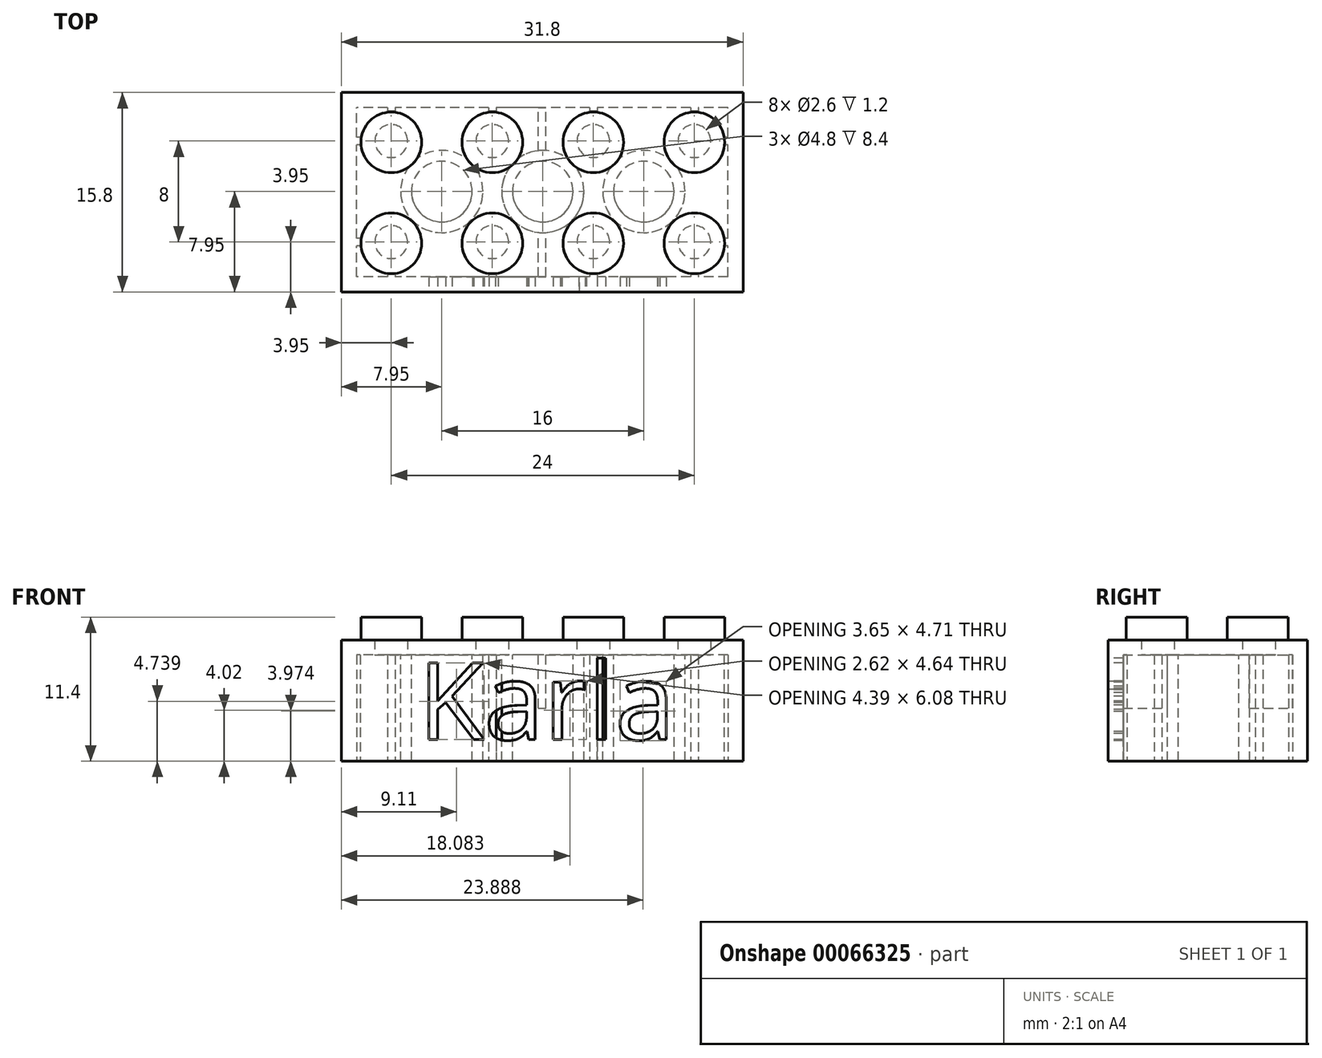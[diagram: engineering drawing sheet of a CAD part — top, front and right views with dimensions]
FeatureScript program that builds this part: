
annotation { "Feature Type Name" : "Feature", "Feature Type Description" : "" }
export const myFeature = defineFeature(function(context is Context, id is Id, definition is map)
    precondition{}
    {
        {
            var Q0;
            Q0=qCreatedBy(makeId("Top.planeOp"),FACE);
            var sketch = newSketch(context, id + "F0", { "sketchPlane" : qUnion([Q0])});
            skLineSegment(sketch, "E0.rect.bottom", {"start": v(15.9, 7.9) * mm, "end": v(-15.9, 7.9) * mm});
            skLineSegment(sketch, "E0.rect.top", {"start": v(15.9, -7.9) * mm, "end": v(-15.9, -7.9) * mm});
            skLineSegment(sketch, "E0.rect.left", {"start": v(15.9, 7.9) * mm, "end": v(15.9, -7.9) * mm});
            skLineSegment(sketch, "E0.rect.right", {"start": v(-15.9, 7.9) * mm, "end": v(-15.9, -7.9) * mm});
            skPoint(sketch, "E0.rect.middle", {"position": v(0, 0) * mm});
            skSolve(sketch);
        }
        {
            var Q0;
            Q0 = qSketchRegion(id + "F0", true);
            extrude(context, id + "F1", {"entities" : qUnion([Q0]), "depth" : 9.6 * mm});
        }
        {
            var Q0;
            Q0=makeQuery(id+"F1.opExtrude","CAP_FACE",FACE,{"disambiguationData":[OSD([sQuery(id+"F0.wireOp",EDGE,"E0.rect.bottom"),sQuery(id+"F0.wireOp",EDGE,"E0.rect.top"),sQuery(id+"F0.wireOp",EDGE,"E0.rect.left"),sQuery(id+"F0.wireOp",EDGE,"E0.rect.right")])],"isStart":true});
            var sketch = newSketch(context, id + "F2", { "sketchPlane" : qUnion([Q0])});
            skLineSegment(sketch, "E1.rect.bottom", {"start": v(14.7, 6.7) * mm, "end": v(-14.7, 6.7) * mm});
            skLineSegment(sketch, "E1.rect.top", {"start": v(14.7, -6.7) * mm, "end": v(-14.7, -6.7) * mm});
            skLineSegment(sketch, "E1.rect.left", {"start": v(14.7, 6.7) * mm, "end": v(14.7, -6.7) * mm});
            skLineSegment(sketch, "E1.rect.right", {"start": v(-14.7, 6.7) * mm, "end": v(-14.7, -6.7) * mm});
            skPoint(sketch, "E1.rect.middle", {"position": v(0, 0) * mm});
            skSolve(sketch);
        }
        {
            var Q0;
            Q0 = qSketchRegion(id + "F2", true);
            extrude(context, id + "F3", {"entities" : qUnion([Q0]), "operationType" : NewBodyOperationType.REMOVE, "oppositeDirection" : true, "depth" : 8.4 * mm});
        }
        {
            var Q0;
            Q0=makeQuery(id+"F1.opExtrude","CAP_FACE",FACE,{"disambiguationData":[OSD([sQuery(id+"F0.wireOp",EDGE,"E0.rect.bottom"),sQuery(id+"F0.wireOp",EDGE,"E0.rect.top"),sQuery(id+"F0.wireOp",EDGE,"E0.rect.left"),sQuery(id+"F0.wireOp",EDGE,"E0.rect.right")])],"isStart":false});
            var sketch = newSketch(context, id + "F4", { "sketchPlane" : qUnion([Q0])});
            skLineSegment(sketch, "E2", {"start": v(-26.48, 0) * mm, "end": v(22.09, 0) * mm, "construction": true});
            skCircle(sketch, "E3", {"center": v(-11.95, 3.95) * mm, "radius": 2.4 * mm});
            skCircle(sketch, "E4.0.1.0", {"center": v(-11.95, -4.05) * mm, "radius": 2.4 * mm});
            skCircle(sketch, "E4.1.0.0", {"center": v(-3.95, 3.95) * mm, "radius": 2.4 * mm});
            skCircle(sketch, "E4.1.1.0", {"center": v(-3.95, -4.05) * mm, "radius": 2.4 * mm});
            skCircle(sketch, "E4.2.0.0", {"center": v(4.05, 3.95) * mm, "radius": 2.4 * mm});
            skCircle(sketch, "E4.2.1.0", {"center": v(4.05, -4.05) * mm, "radius": 2.4 * mm});
            skCircle(sketch, "E4.3.0.0", {"center": v(12.05, 3.95) * mm, "radius": 2.4 * mm});
            skCircle(sketch, "E4.3.1.0", {"center": v(12.05, -4.05) * mm, "radius": 2.4 * mm});
            skLineSegment(sketch, "E4.direction1", {"start": v(-11.95, 3.95) * mm, "end": v(-3.95, 3.95) * mm, "construction": true});
            skLineSegment(sketch, "E4.direction2", {"start": v(-11.95, 3.95) * mm, "end": v(-11.95, -4.05) * mm, "construction": true});
            skSolve(sketch);
        }
        {
            var Q0;
            Q0 = qSketchRegion(id + "F4", true);
            extrude(context, id + "F5", {"entities" : qUnion([Q0]), "operationType" : NewBodyOperationType.ADD, "depth" : 1.8 * mm});
        }
        {
            var Q0;
            Q0=makeQuery(id+"F3.boolean.opBoolean","COPY",FACE,{"derivedFrom":makeQuery(id+"F3.opExtrude","CAP_FACE",FACE,{"disambiguationData":[OSD([sQuery(id+"F2.wireOp",EDGE,"E1.rect.bottom"),sQuery(id+"F2.wireOp",EDGE,"E1.rect.top"),sQuery(id+"F2.wireOp",EDGE,"E1.rect.left"),sQuery(id+"F2.wireOp",EDGE,"E1.rect.right")])],"isStart":false})});
            var sketch = newSketch(context, id + "F6", { "sketchPlane" : qUnion([Q0])});
            skCircle(sketch, "E5", {"center": v(-11.95, 3.95) * mm, "radius": 1.3 * mm});
            skCircle(sketch, "E6.0.1.0", {"center": v(-11.95, -4.05) * mm, "radius": 1.3 * mm});
            skCircle(sketch, "E6.1.0.0", {"center": v(-3.95, 3.95) * mm, "radius": 1.3 * mm});
            skCircle(sketch, "E6.1.1.0", {"center": v(-3.95, -4.05) * mm, "radius": 1.3 * mm});
            skCircle(sketch, "E6.2.0.0", {"center": v(4.05, 3.95) * mm, "radius": 1.3 * mm});
            skCircle(sketch, "E6.2.1.0", {"center": v(4.05, -4.05) * mm, "radius": 1.3 * mm});
            skCircle(sketch, "E6.3.0.0", {"center": v(12.05, 3.95) * mm, "radius": 1.3 * mm});
            skCircle(sketch, "E6.3.1.0", {"center": v(12.05, -4.05) * mm, "radius": 1.3 * mm});
            skLineSegment(sketch, "E6.direction1", {"start": v(-11.95, 3.95) * mm, "end": v(-3.95, 3.95) * mm, "construction": true});
            skLineSegment(sketch, "E6.direction2", {"start": v(-11.95, 3.95) * mm, "end": v(-11.95, -4.05) * mm, "construction": true});
            skSolve(sketch);
        }
        {
            var Q0;
            Q0 = qSketchRegion(id + "F6", true);
            extrude(context, id + "F7", {"entities" : qUnion([Q0]), "operationType" : NewBodyOperationType.REMOVE, "oppositeDirection" : true, "depth" : 1.2 * mm});
        }
        {
            var Q0;
            Q0=makeQuery(id+"F3.boolean.opBoolean","COPY",FACE,{"derivedFrom":makeQuery(id+"F3.opExtrude","CAP_FACE",FACE,{"disambiguationData":[OSD([sQuery(id+"F2.wireOp",EDGE,"E1.rect.bottom"),sQuery(id+"F2.wireOp",EDGE,"E1.rect.top"),sQuery(id+"F2.wireOp",EDGE,"E1.rect.left"),sQuery(id+"F2.wireOp",EDGE,"E1.rect.right")])],"isStart":false})});
            var sketch = newSketch(context, id + "F8", { "sketchPlane" : qUnion([Q0])});
            skLineSegment(sketch, "E7", {"start": v(-11.95, 3.95) * mm, "end": v(-3.95, -4.05) * mm, "construction": true});
            skLineSegment(sketch, "E8", {"start": v(-3.95, 3.95) * mm, "end": v(-11.95, -4.05) * mm, "construction": true});
            skLineSegment(sketch, "E9", {"start": v(4.05, 3.95) * mm, "end": v(12.05, -4.05) * mm, "construction": true});
            skLineSegment(sketch, "E10", {"start": v(4.05, -4.05) * mm, "end": v(12.05, 3.95) * mm, "construction": true});
            skLineSegment(sketch, "E11", {"start": v(-3.95, 3.95) * mm, "end": v(4.05, -4.05) * mm, "construction": true});
            skLineSegment(sketch, "E12", {"start": v(-3.95, -4.05) * mm, "end": v(4.05, 3.95) * mm, "construction": true});
            skCircle(sketch, "E13", {"center": v(-7.95, -0.05) * mm, "radius": 2.4 * mm});
            skCircle(sketch, "E14", {"center": v(-7.95, -0.05) * mm, "radius": 3.25 * mm});
            skCircle(sketch, "E15", {"center": v(0.05, -0.05) * mm, "radius": 2.4 * mm});
            skCircle(sketch, "E16", {"center": v(0.05, -0.05) * mm, "radius": 3.25 * mm});
            skCircle(sketch, "E17", {"center": v(8.05, -0.05) * mm, "radius": 2.4 * mm});
            skCircle(sketch, "E18", {"center": v(8.05, -0.05) * mm, "radius": 3.25 * mm});
            skSolve(sketch);
        }
        {
            var Q0;
            Q0 = qSketchRegion(id + "F8", true);
            var Q1;
            Q1=makeQuery(id+"F1.opExtrude","CAP_FACE",FACE,{"disambiguationData":[OSD([sQuery(id+"F0.wireOp",EDGE,"E0.rect.bottom"),sQuery(id+"F0.wireOp",EDGE,"E0.rect.top"),sQuery(id+"F0.wireOp",EDGE,"E0.rect.left"),sQuery(id+"F0.wireOp",EDGE,"E0.rect.right")])],"isStart":true});
            extrude(context, id + "F9", {"entities" : qUnion([Q0]), "operationType" : NewBodyOperationType.ADD, "endBound" : BoundingType.UP_TO_SURFACE, "endBoundEntityFace" : qUnion([Q1]), "depth" : 25 * mm});
        }
        {
            var Q0;
            Q0=makeQuery(id+"F1.opExtrude","CAP_FACE",FACE,{"disambiguationData":[OSD([sQuery(id+"F0.wireOp",EDGE,"E0.rect.bottom"),sQuery(id+"F0.wireOp",EDGE,"E0.rect.top"),sQuery(id+"F0.wireOp",EDGE,"E0.rect.left"),sQuery(id+"F0.wireOp",EDGE,"E0.rect.right")])],"isStart":true});
            var sketch = newSketch(context, id + "F10", { "sketchPlane" : qUnion([Q0])});
            skLineSegment(sketch, "E19.bottom", {"start": v(-12.25, 6.7) * mm, "end": v(-11.65, 6.7) * mm});
            skLineSegment(sketch, "E19.top", {"start": v(-12.25, 6.4) * mm, "end": v(-11.65, 6.4) * mm});
            skLineSegment(sketch, "E19.left", {"start": v(-12.25, 6.7) * mm, "end": v(-12.25, 6.4) * mm});
            skLineSegment(sketch, "E19.right", {"start": v(-11.65, 6.7) * mm, "end": v(-11.65, 6.4) * mm});
            skLineSegment(sketch, "E20.0.1.0", {"start": v(-12.25, -6.4) * mm, "end": v(-11.65, -6.4) * mm});
            skLineSegment(sketch, "E20.0.1.1", {"start": v(-12.25, -6.4) * mm, "end": v(-12.25, -6.7) * mm});
            skLineSegment(sketch, "E20.0.1.2", {"start": v(-12.25, -6.7) * mm, "end": v(-11.65, -6.7) * mm});
            skLineSegment(sketch, "E20.0.1.3", {"start": v(-11.65, -6.4) * mm, "end": v(-11.65, -6.7) * mm});
            skLineSegment(sketch, "E20.1.0.0", {"start": v(-4.25, 6.7) * mm, "end": v(-3.65, 6.7) * mm});
            skLineSegment(sketch, "E20.1.0.1", {"start": v(-4.25, 6.7) * mm, "end": v(-4.25, 6.4) * mm});
            skLineSegment(sketch, "E20.1.0.2", {"start": v(-4.25, 6.4) * mm, "end": v(-3.65, 6.4) * mm});
            skLineSegment(sketch, "E20.1.0.3", {"start": v(-3.65, 6.7) * mm, "end": v(-3.65, 6.4) * mm});
            skLineSegment(sketch, "E20.1.1.0", {"start": v(-4.25, -6.4) * mm, "end": v(-3.65, -6.4) * mm});
            skLineSegment(sketch, "E20.1.1.1", {"start": v(-4.25, -6.4) * mm, "end": v(-4.25, -6.7) * mm});
            skLineSegment(sketch, "E20.1.1.2", {"start": v(-4.25, -6.7) * mm, "end": v(-3.65, -6.7) * mm});
            skLineSegment(sketch, "E20.1.1.3", {"start": v(-3.65, -6.4) * mm, "end": v(-3.65, -6.7) * mm});
            skLineSegment(sketch, "E20.2.0.0", {"start": v(3.75, 6.7) * mm, "end": v(4.35, 6.7) * mm});
            skLineSegment(sketch, "E20.2.0.1", {"start": v(3.75, 6.7) * mm, "end": v(3.75, 6.4) * mm});
            skLineSegment(sketch, "E20.2.0.2", {"start": v(3.75, 6.4) * mm, "end": v(4.35, 6.4) * mm});
            skLineSegment(sketch, "E20.2.0.3", {"start": v(4.35, 6.7) * mm, "end": v(4.35, 6.4) * mm});
            skLineSegment(sketch, "E20.2.1.0", {"start": v(3.75, -6.4) * mm, "end": v(4.35, -6.4) * mm});
            skLineSegment(sketch, "E20.2.1.1", {"start": v(3.75, -6.4) * mm, "end": v(3.75, -6.7) * mm});
            skLineSegment(sketch, "E20.2.1.2", {"start": v(3.75, -6.7) * mm, "end": v(4.35, -6.7) * mm});
            skLineSegment(sketch, "E20.2.1.3", {"start": v(4.35, -6.4) * mm, "end": v(4.35, -6.7) * mm});
            skLineSegment(sketch, "E20.3.0.0", {"start": v(11.75, 6.7) * mm, "end": v(12.35, 6.7) * mm});
            skLineSegment(sketch, "E20.3.0.1", {"start": v(11.75, 6.7) * mm, "end": v(11.75, 6.4) * mm});
            skLineSegment(sketch, "E20.3.0.2", {"start": v(11.75, 6.4) * mm, "end": v(12.35, 6.4) * mm});
            skLineSegment(sketch, "E20.3.0.3", {"start": v(12.35, 6.7) * mm, "end": v(12.35, 6.4) * mm});
            skLineSegment(sketch, "E20.3.1.0", {"start": v(11.75, -6.4) * mm, "end": v(12.35, -6.4) * mm});
            skLineSegment(sketch, "E20.3.1.1", {"start": v(11.75, -6.4) * mm, "end": v(11.75, -6.7) * mm});
            skLineSegment(sketch, "E20.3.1.2", {"start": v(11.75, -6.7) * mm, "end": v(12.35, -6.7) * mm});
            skLineSegment(sketch, "E20.3.1.3", {"start": v(12.35, -6.4) * mm, "end": v(12.35, -6.7) * mm});
            skLineSegment(sketch, "E20.direction1", {"start": v(-12.25, 6.7) * mm, "end": v(-4.25, 6.7) * mm, "construction": true});
            skLineSegment(sketch, "E20.direction2", {"start": v(-12.25, 6.7) * mm, "end": v(-12.25, -6.4) * mm, "construction": true});
            skSolve(sketch);
        }
        {
            var Q0;
            Q0 = qSketchRegion(id + "F10", true);
            var Q1;
            {var subQ0=sQuery(id+"F2.wireOp",EDGE,"E1.rect.bottom");var subQ1=sQuery(id+"F2.wireOp",EDGE,"E1.rect.top");var subQ2=sQuery(id+"F2.wireOp",EDGE,"E1.rect.left");var subQ3=sQuery(id+"F2.wireOp",EDGE,"E1.rect.right");Q1=makeQuery(id+"F9.boolean.opBoolean","SPLIT",FACE,{"disambiguationData":[TD([makeQuery(id+"F3.boolean.opBoolean","COPY",FACE,{"derivedFrom":makeQuery(id+"F3.opExtrude","SWEPT_FACE",FACE,{"disambiguationData":[OSD([subQ0])]})})])],"derivedFrom":makeQuery(id+"F3.boolean.opBoolean","COPY",FACE,{"derivedFrom":makeQuery(id+"F3.opExtrude","CAP_FACE",FACE,{"disambiguationData":[OSD([subQ0,subQ1,subQ2,subQ3])],"isStart":false})})});}
            extrude(context, id + "F11", {"entities" : qUnion([Q0]), "operationType" : NewBodyOperationType.ADD, "endBound" : BoundingType.UP_TO_SURFACE, "oppositeDirection" : true, "endBoundEntityFace" : qUnion([Q1]), "depth" : 25 * mm});
        }
        {
            var Q0;
            Q0=makeQuery(id+"F11.boolean.opBoolean","MERGE",FACE,{"derivedFrom":[makeQuery(id+"F1.opExtrude","CAP_FACE",FACE,{"disambiguationData":[OSD([sQuery(id+"F0.wireOp",EDGE,"E0.rect.bottom"),sQuery(id+"F0.wireOp",EDGE,"E0.rect.top"),sQuery(id+"F0.wireOp",EDGE,"E0.rect.left"),sQuery(id+"F0.wireOp",EDGE,"E0.rect.right")])],"isStart":true}),makeQuery(id+"F11.opExtrude","CAP_FACE",FACE,{"disambiguationData":[OSD([sQuery(id+"F10.wireOp",EDGE,"E19.bottom"),sQuery(id+"F10.wireOp",EDGE,"E19.top"),sQuery(id+"F10.wireOp",EDGE,"E19.left"),sQuery(id+"F10.wireOp",EDGE,"E19.right")])],"isStart":true}),makeQuery(id+"F11.opExtrude","CAP_FACE",FACE,{"disambiguationData":[OSD([sQuery(id+"F10.wireOp",EDGE,"E20.0.1.0"),sQuery(id+"F10.wireOp",EDGE,"E20.0.1.1"),sQuery(id+"F10.wireOp",EDGE,"E20.0.1.2"),sQuery(id+"F10.wireOp",EDGE,"E20.0.1.3")])],"isStart":true}),makeQuery(id+"F11.opExtrude","CAP_FACE",FACE,{"disambiguationData":[OSD([sQuery(id+"F10.wireOp",EDGE,"E20.1.0.0"),sQuery(id+"F10.wireOp",EDGE,"E20.1.0.1"),sQuery(id+"F10.wireOp",EDGE,"E20.1.0.2"),sQuery(id+"F10.wireOp",EDGE,"E20.1.0.3")])],"isStart":true}),makeQuery(id+"F11.opExtrude","CAP_FACE",FACE,{"disambiguationData":[OSD([sQuery(id+"F10.wireOp",EDGE,"E20.1.1.0"),sQuery(id+"F10.wireOp",EDGE,"E20.1.1.1"),sQuery(id+"F10.wireOp",EDGE,"E20.1.1.2"),sQuery(id+"F10.wireOp",EDGE,"E20.1.1.3")])],"isStart":true}),makeQuery(id+"F11.opExtrude","CAP_FACE",FACE,{"disambiguationData":[OSD([sQuery(id+"F10.wireOp",EDGE,"E20.2.0.0"),sQuery(id+"F10.wireOp",EDGE,"E20.2.0.1"),sQuery(id+"F10.wireOp",EDGE,"E20.2.0.2"),sQuery(id+"F10.wireOp",EDGE,"E20.2.0.3")])],"isStart":true}),makeQuery(id+"F11.opExtrude","CAP_FACE",FACE,{"disambiguationData":[OSD([sQuery(id+"F10.wireOp",EDGE,"E20.2.1.0"),sQuery(id+"F10.wireOp",EDGE,"E20.2.1.1"),sQuery(id+"F10.wireOp",EDGE,"E20.2.1.2"),sQuery(id+"F10.wireOp",EDGE,"E20.2.1.3")])],"isStart":true}),makeQuery(id+"F11.opExtrude","CAP_FACE",FACE,{"disambiguationData":[OSD([sQuery(id+"F10.wireOp",EDGE,"E20.3.0.0"),sQuery(id+"F10.wireOp",EDGE,"E20.3.0.1"),sQuery(id+"F10.wireOp",EDGE,"E20.3.0.2"),sQuery(id+"F10.wireOp",EDGE,"E20.3.0.3")])],"isStart":true}),makeQuery(id+"F11.opExtrude","CAP_FACE",FACE,{"disambiguationData":[OSD([sQuery(id+"F10.wireOp",EDGE,"E20.3.1.0"),sQuery(id+"F10.wireOp",EDGE,"E20.3.1.1"),sQuery(id+"F10.wireOp",EDGE,"E20.3.1.2"),sQuery(id+"F10.wireOp",EDGE,"E20.3.1.3")])],"isStart":true})]});
            var sketch = newSketch(context, id + "F12", { "sketchPlane" : qUnion([Q0])});
            skLineSegment(sketch, "E21.bottom", {"start": v(-14.7, 4.25) * mm, "end": v(-14.4, 4.25) * mm});
            skLineSegment(sketch, "E21.top", {"start": v(-14.7, 3.65) * mm, "end": v(-14.4, 3.65) * mm});
            skLineSegment(sketch, "E21.left", {"start": v(-14.7, 4.25) * mm, "end": v(-14.7, 3.65) * mm});
            skLineSegment(sketch, "E21.right", {"start": v(-14.4, 4.25) * mm, "end": v(-14.4, 3.65) * mm});
            skLineSegment(sketch, "E22.0.1.0", {"start": v(-14.7, -3.75) * mm, "end": v(-14.7, -4.35) * mm});
            skLineSegment(sketch, "E22.0.1.1", {"start": v(-14.7, -3.75) * mm, "end": v(-14.4, -3.75) * mm});
            skLineSegment(sketch, "E22.0.1.2", {"start": v(-14.4, -3.75) * mm, "end": v(-14.4, -4.35) * mm});
            skLineSegment(sketch, "E22.0.1.3", {"start": v(-14.7, -4.35) * mm, "end": v(-14.4, -4.35) * mm});
            skLineSegment(sketch, "E22.1.0.0", {"start": v(14.4, 4.25) * mm, "end": v(14.4, 3.65) * mm});
            skLineSegment(sketch, "E22.1.0.1", {"start": v(14.4, 4.25) * mm, "end": v(14.7, 4.25) * mm});
            skLineSegment(sketch, "E22.1.0.2", {"start": v(14.7, 4.25) * mm, "end": v(14.7, 3.65) * mm});
            skLineSegment(sketch, "E22.1.0.3", {"start": v(14.4, 3.65) * mm, "end": v(14.7, 3.65) * mm});
            skLineSegment(sketch, "E22.1.1.0", {"start": v(14.4, -3.75) * mm, "end": v(14.4, -4.35) * mm});
            skLineSegment(sketch, "E22.1.1.1", {"start": v(14.4, -3.75) * mm, "end": v(14.7, -3.75) * mm});
            skLineSegment(sketch, "E22.1.1.2", {"start": v(14.7, -3.75) * mm, "end": v(14.7, -4.35) * mm});
            skLineSegment(sketch, "E22.1.1.3", {"start": v(14.4, -4.35) * mm, "end": v(14.7, -4.35) * mm});
            skLineSegment(sketch, "E22.direction1", {"start": v(-14.7, 3.65) * mm, "end": v(14.4, 3.65) * mm, "construction": true});
            skLineSegment(sketch, "E22.direction2", {"start": v(-14.7, 3.65) * mm, "end": v(-14.7, -4.35) * mm, "construction": true});
            skSolve(sketch);
        }
        {
            var Q0;
            Q0 = qSketchRegion(id + "F12", true);
            var Q1;
            {var subQ0=sQuery(id+"F2.wireOp",EDGE,"E1.rect.bottom");var subQ1=sQuery(id+"F2.wireOp",EDGE,"E1.rect.top");var subQ2=sQuery(id+"F2.wireOp",EDGE,"E1.rect.left");var subQ3=sQuery(id+"F2.wireOp",EDGE,"E1.rect.right");Q1=makeQuery(id+"F9.boolean.opBoolean","SPLIT",FACE,{"disambiguationData":[TD([makeQuery(id+"F3.boolean.opBoolean","COPY",FACE,{"derivedFrom":makeQuery(id+"F3.opExtrude","SWEPT_FACE",FACE,{"disambiguationData":[OSD([subQ0])]})})])],"derivedFrom":makeQuery(id+"F3.boolean.opBoolean","COPY",FACE,{"derivedFrom":makeQuery(id+"F3.opExtrude","CAP_FACE",FACE,{"disambiguationData":[OSD([subQ0,subQ1,subQ2,subQ3])],"isStart":false})})});}
            extrude(context, id + "F13", {"entities" : qUnion([Q0]), "operationType" : NewBodyOperationType.ADD, "endBound" : BoundingType.UP_TO_SURFACE, "oppositeDirection" : true, "endBoundEntityFace" : qUnion([Q1]), "depth" : 25 * mm});
        }
        {
            var Q0;
            Q0=makeQuery(id+"F8.imprint","IMPRINT",FACE,{"disambiguationData":[TD([[makeQuery(id+"F8.imprint","IMPRINT",EDGE,{"derivedFrom":sQuery(id+"F8.wireOp",EDGE,"E14")}),-1.0]])]});
            var sketch = newSketch(context, id + "F14", { "sketchPlane" : qUnion([Q0])});
            skLineSegment(sketch, "E23.bottom", {"start": v(-0.3, 6.95) * mm, "end": v(0.3, 6.95) * mm});
            skLineSegment(sketch, "E23.top", {"start": v(-0.3, 2.7) * mm, "end": v(0.3, 2.7) * mm});
            skLineSegment(sketch, "E23.left", {"start": v(-0.3, 6.95) * mm, "end": v(-0.3, 2.7) * mm});
            skLineSegment(sketch, "E23.right", {"start": v(0.3, 6.95) * mm, "end": v(0.3, 2.7) * mm});
            skLineSegment(sketch, "E24.bottom", {"start": v(-0.3, -2.7) * mm, "end": v(0.3, -2.7) * mm});
            skLineSegment(sketch, "E24.top", {"start": v(-0.3, -6.95) * mm, "end": v(0.3, -6.95) * mm});
            skLineSegment(sketch, "E24.left", {"start": v(-0.3, -2.7) * mm, "end": v(-0.3, -6.95) * mm});
            skLineSegment(sketch, "E24.right", {"start": v(0.3, -2.7) * mm, "end": v(0.3, -6.95) * mm});
            skSolve(sketch);
        }
        {
            var Q0;
            Q0 = qSketchRegion(id + "F14", true);
            extrude(context, id + "F15", {"entities" : qUnion([Q0]), "operationType" : NewBodyOperationType.ADD, "depth" : 4.2 * mm});
        }
        {
            var Q0;
            Q0=makeQuery(id+"F1.opExtrude","SWEPT_FACE",FACE,{"disambiguationData":[OSD([sQuery(id+"F0.wireOp",EDGE,"E0.rect.top")])]});
            var sketch = newSketch(context, id + "F16", { "sketchPlane" : qUnion([Q0])});
            skText(sketch, "E25", { "text": "Karla", "fontName": "OpenSans-Regular.ttf"});
            const initialGuessF16  = {"E25": [-0.00982, 0.0017, 1, 0, 0.00613]};
            skSetInitialGuess(sketch, initialGuessF16);
            skSolve(sketch);
        }
        {
            var Q0;
            Q0 = qSketchRegion(id + "F16", true);
            extrude(context, id + "F17", {"entities" : qUnion([Q0]), "operationType" : NewBodyOperationType.REMOVE, "oppositeDirection" : true, "depth" : 1.2 * mm});
        }
    });
